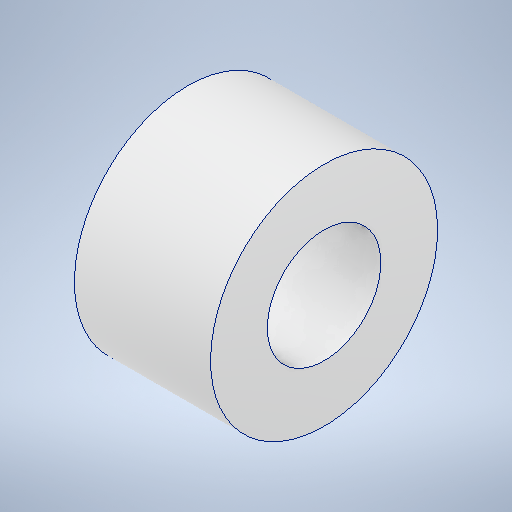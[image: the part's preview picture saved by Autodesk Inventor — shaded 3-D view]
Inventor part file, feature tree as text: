
AUTODESK INVENTOR PART (.ipt)
format: ipt  version: 2025.1 (Build 291241020, 241B)  size: 225,792 bytes
history: native  units: mm
features: extrude x1, sketch x1
ambient origin geometry x8: Origin, YZ Plane, XZ Plane, XY Plane, X Axis, Y Axis, Z Axis, Center Point
bodies: Solid1 (feature_tree)
feature tree (2):
  extrude  "Extrusion1"  Depth=10.0mm
  sketch  "Sketch1"  dims[d0=5.0mm d1=10.0mm d2=6.0mm d3=0.0mm]
